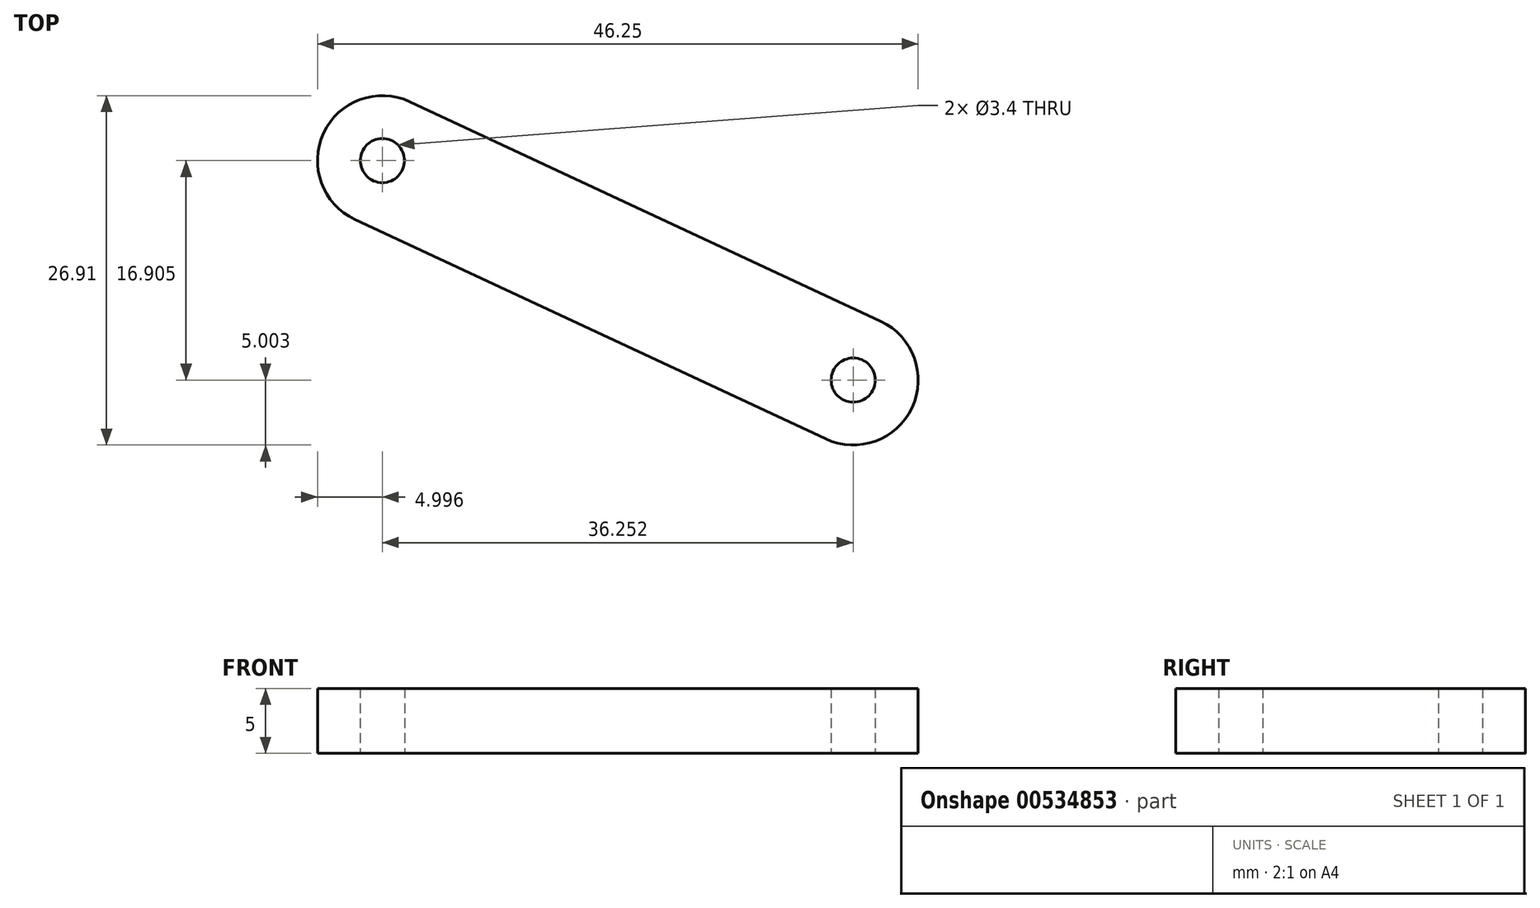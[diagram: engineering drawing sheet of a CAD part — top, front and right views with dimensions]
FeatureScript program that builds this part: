
annotation { "Feature Type Name" : "Feature", "Feature Type Description" : "" }
export const myFeature = defineFeature(function(context is Context, id is Id, definition is map)
    precondition{}
    {
        {
            var Q0;
            Q0=qCreatedBy(makeId("Top.planeOp"),FACE);
            var sketch = newSketch(context, id + "F0", { "sketchPlane" : qUnion([Q0])});
            skLineSegment(sketch, "E0.left", {"start": v(-52.76, 28.84) * mm, "end": v(-52.76, -11.16) * mm});
            skLineSegment(sketch, "E0.right", {"start": v(-42.76, 28.84) * mm, "end": v(-42.76, -11.16) * mm});
            skArc(sketch, "E1", {"start": v(-52.76, 28.84) * mm, "mid": v(-47.76, 33.84) * mm, "end": v(-42.76, 28.84) * mm});
            skArc(sketch, "E2", {"start": v(-52.76, -11.16) * mm, "mid": v(-47.76, -16.16) * mm, "end": v(-42.76, -11.16) * mm});
            skCircle(sketch, "E3", {"center": v(-47.76, -11.16) * mm, "radius": 1.7 * mm});
            skCircle(sketch, "E4", {"center": v(-47.76, 28.84) * mm, "radius": 1.7 * mm});
            skLineSegment(sketch, "E5", {"start": v(-52.76, -5.66) * mm, "end": v(-42.76, -5.66) * mm});
            skSolve(sketch);
        }
        {
            var Q0;
            Q0=qSketchRegion(id+"F0",true);
            extrude(context, id + "F1", {"entities" : qUnion([Q0]), "depth" : 5 * mm});
        }
        {
            var Q0;
            Q0=makeQuery(id+"F1.opExtrude","SWEPT_BODY",BODY,{"disambiguationData":[OSD([sQuery(id+"F0.wireOp",EDGE,"E0.left"),sQuery(id+"F0.wireOp",EDGE,"E0.right"),sQuery(id+"F0.wireOp",EDGE,"E1"),sQuery(id+"F0.wireOp",EDGE,"E2"),sQuery(id+"F0.wireOp",EDGE,"E3"),sQuery(id+"F0.wireOp",EDGE,"E4")])]});
            var Q1;
            Q1=makeQuery(id+"F1.opExtrude","CAP_EDGE",EDGE,{"disambiguationData":[OSD([sQuery(id+"F0.wireOp",EDGE,"E3")])],"isStart":false});
            transform(context, id + "F2", {"entities" : qUnion([Q0]), "transformType" : TransformType.ROTATION, "transformAxis" : qUnion([Q1]), "angle" : 115 * degree, "oppositeDirection" : true, "makeCopy" : false});
        }
    });
